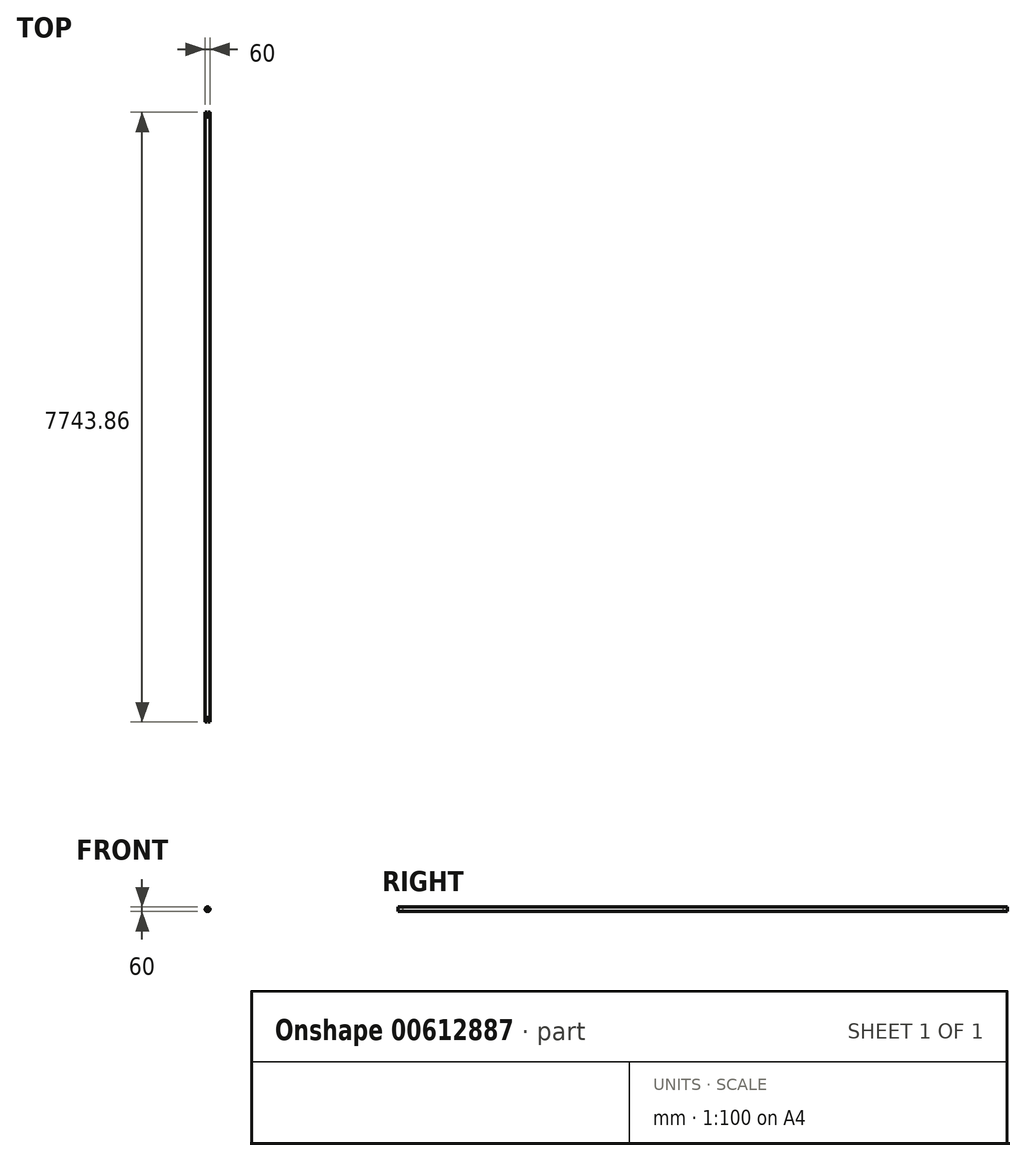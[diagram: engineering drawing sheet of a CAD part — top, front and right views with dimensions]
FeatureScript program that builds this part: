
annotation { "Feature Type Name" : "Feature", "Feature Type Description" : "" }
export const myFeature = defineFeature(function(context is Context, id is Id, definition is map)
    precondition{}
    {
        {
            var Q0;
            Q0=qCreatedBy(makeId("Front.planeOp"),FACE);
            var sketch = newSketch(context, id + "F0", { "sketchPlane" : qUnion([Q0])});
            skCircle(sketch, "E0", {"center": v(0, 0) * mm, "radius": 30 * mm});
            skSolve(sketch);
        }
        {
            var Q0;
            Q0=makeQuery(id+"F0.imprint","IMPRINT",FACE,{"disambiguationData":[TD([[makeQuery(id+"F0.imprint","IMPRINT",EDGE,{"derivedFrom":sQuery(id+"F0.wireOp",EDGE,"E0")}),1.0]])]});
            extrude(context, id + "F1", {"entities" : qUnion([Q0]), "endBound" : BoundingType.SYMMETRIC, "depth" : ((((7590 + 36 + 16) + 200) - 178.76) + 80.62) * mm, "offsetDistance" : 25 * mm});
        }
        {
            var Q0;
            Q0=makeQuery(id+"F1.opExtrude","CAP_FACE",FACE,{"disambiguationData":[OSD([sQuery(id+"F0.wireOp",EDGE,"E0")])],"isStart":false});
            var sketch = newSketch(context, id + "F2", { "sketchPlane" : qUnion([Q0])});
            skLineSegment(sketch, "E1.bottom", {"start": v(6, 92.55) * mm, "end": v(-6, 92.55) * mm});
            skLineSegment(sketch, "E1.top", {"start": v(6, -92.55) * mm, "end": v(-6, -92.55) * mm});
            skLineSegment(sketch, "E1.left", {"start": v(6, 92.55) * mm, "end": v(6, -92.55) * mm});
            skLineSegment(sketch, "E1.right", {"start": v(-6, 92.55) * mm, "end": v(-6, -92.55) * mm});
            skPoint(sketch, "E1.middle", {"position": v(0, 0) * mm});
            skSolve(sketch);
        }
        {
            var Q0;
            {var subQ0=sQuery(id+"F2.wireOp",EDGE,"E1.bottom");Q0=makeQuery(id+"F2.imprint","IMPRINT",FACE,{"disambiguationData":[TD([[makeQuery(id+"F2.imprint","IMPRINT",EDGE,{"derivedFrom":subQ0}),1.0]])]});}
            var Q1;
            {var subQ0=sQuery(id+"F2.wireOp",EDGE,"E1.left");var subQ1=makeQuery(id+"F1.opExtrude","CAP_EDGE",EDGE,{"disambiguationData":[OSD([sQuery(id+"F0.wireOp",EDGE,"E0")])],"isStart":false});var subQ2=makeQuery(id+"F2.imprint","INTERSECT",VERTEX,{"disambiguationData":[OD(0.0)],"derivedFrom":[subQ1,subQ0]});Q1=makeQuery(id+"F2.imprint","IMPRINT",FACE,{"disambiguationData":[TD([[makeQuery(id+"F2.imprint","IMPRINT",EDGE,{"disambiguationData":[TD([[subQ2,-1.0]])],"derivedFrom":subQ0}),-1.0]])]});}
            extrude(context, id + "F3", {"entities" : qUnion([Q0, Q1]), "operationType" : NewBodyOperationType.REMOVE, "oppositeDirection" : true, "depth" : 60 * mm, "offsetDistance" : 25 * mm});
        }
        {
            var Q0;
            Q0=makeQuery(id+"F1.opExtrude","CAP_FACE",FACE,{"disambiguationData":[OSD([sQuery(id+"F0.wireOp",EDGE,"E0")])],"isStart":true});
            var sketch = newSketch(context, id + "F4", { "sketchPlane" : qUnion([Q0])});
            skLineSegment(sketch, "E2.bottom", {"start": v(5, 59.2) * mm, "end": v(-5, 59.2) * mm});
            skLineSegment(sketch, "E2.top", {"start": v(5, -59.2) * mm, "end": v(-5, -59.2) * mm});
            skLineSegment(sketch, "E2.left", {"start": v(5, 59.2) * mm, "end": v(5, -59.2) * mm});
            skLineSegment(sketch, "E2.right", {"start": v(-5, 59.2) * mm, "end": v(-5, -59.2) * mm});
            skPoint(sketch, "E2.middle", {"position": v(0, 0) * mm});
            skSolve(sketch);
        }
        {
            var Q0;
            {var subQ0=sQuery(id+"F4.wireOp",EDGE,"E2.left");var subQ1=makeQuery(id+"F1.opExtrude","CAP_EDGE",EDGE,{"disambiguationData":[OSD([sQuery(id+"F0.wireOp",EDGE,"E0")])],"isStart":true});var subQ2=makeQuery(id+"F4.imprint","INTERSECT",VERTEX,{"disambiguationData":[OD(0.0)],"derivedFrom":[subQ1,subQ0]});Q0=makeQuery(id+"F4.imprint","IMPRINT",FACE,{"disambiguationData":[TD([[makeQuery(id+"F4.imprint","IMPRINT",EDGE,{"disambiguationData":[TD([[subQ2,-1.0]])],"derivedFrom":subQ0}),-1.0]])]});}
            extrude(context, id + "F5", {"entities" : qUnion([Q0]), "operationType" : NewBodyOperationType.REMOVE, "oppositeDirection" : true, "depth" : 60 * mm, "offsetDistance" : 25 * mm});
        }
    });
